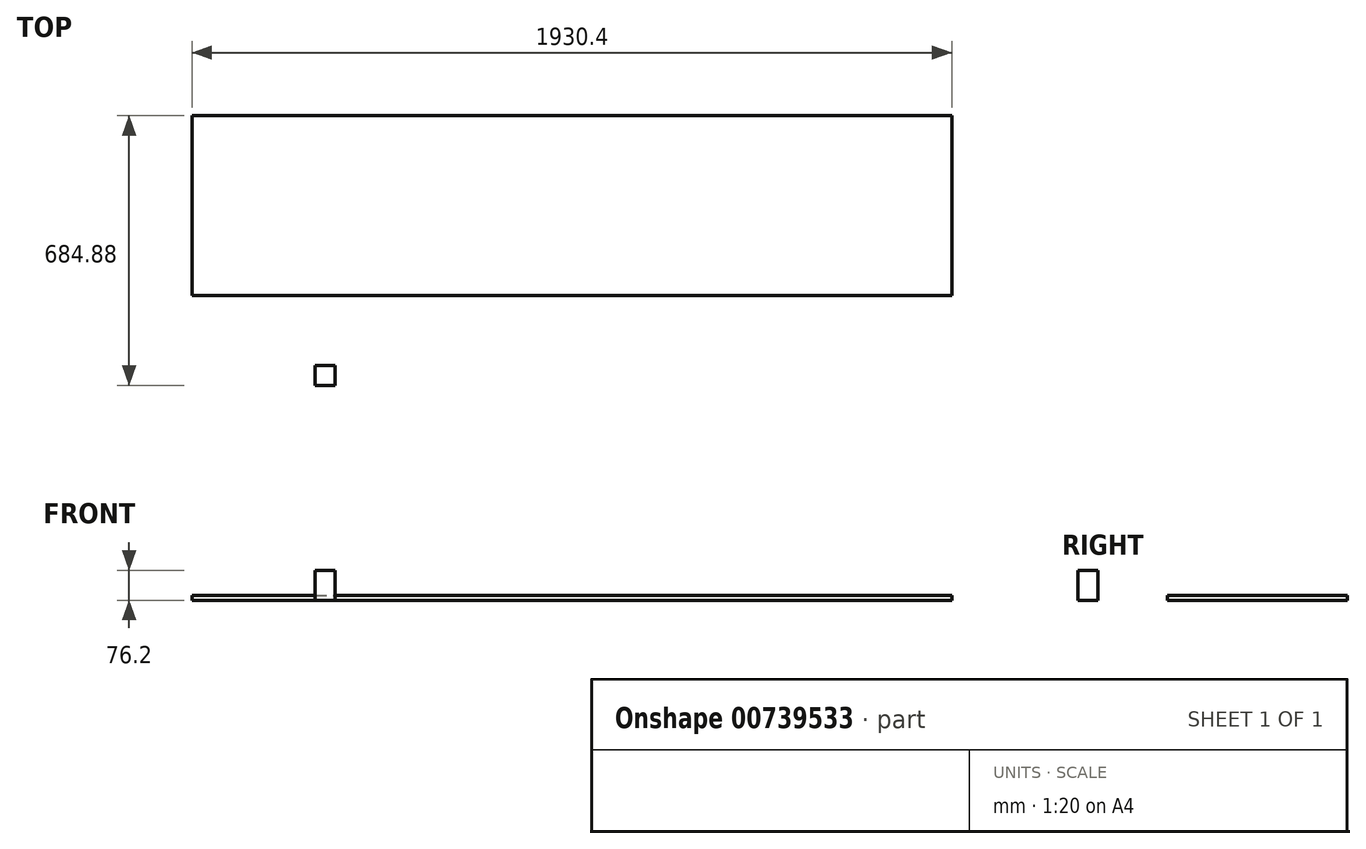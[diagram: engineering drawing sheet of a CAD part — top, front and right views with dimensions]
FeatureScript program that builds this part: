
annotation { "Feature Type Name" : "Feature", "Feature Type Description" : "" }
export const myFeature = defineFeature(function(context is Context, id is Id, definition is map)
    precondition{}
    {
        {
            var Q0;
            Q0=qCreatedBy(makeId("Top.planeOp"),FACE);
            var sketch = newSketch(context, id + "F0", { "sketchPlane" : qUnion([Q0])});
            skLineSegment(sketch, "E0.bottom", {"start": v(-965.2, 228.6) * mm, "end": v(965.2, 228.6) * mm});
            skLineSegment(sketch, "E0.top", {"start": v(-965.2, -228.6) * mm, "end": v(965.2, -228.6) * mm});
            skLineSegment(sketch, "E0.left", {"start": v(-965.2, 228.6) * mm, "end": v(-965.2, -228.6) * mm});
            skLineSegment(sketch, "E0.right", {"start": v(965.2, 228.6) * mm, "end": v(965.2, -228.6) * mm});
            skPoint(sketch, "E0.middle", {"position": v(0, 0) * mm});
            skSolve(sketch);
        }
        {
            var Q0;
            Q0 = qSketchRegion(id + "F0", true);
            extrude(context, id + "F1", {"entities" : qUnion([Q0]), "depth" : 12.7 * mm, "offsetDistance" : 25.4 * mm});
        }
        {
            var Q0;
            Q0=qCreatedBy(makeId("Top.planeOp"),FACE);
            var sketch = newSketch(context, id + "F2", { "sketchPlane" : qUnion([Q0])});
            skLineSegment(sketch, "E1.bottom", {"start": v(-602.16, -456.28) * mm, "end": v(-652.96, -456.28) * mm});
            skLineSegment(sketch, "E1.top", {"start": v(-602.16, -405.48) * mm, "end": v(-652.96, -405.48) * mm});
            skLineSegment(sketch, "E1.left", {"start": v(-602.16, -456.28) * mm, "end": v(-602.16, -405.48) * mm});
            skLineSegment(sketch, "E1.right", {"start": v(-652.96, -456.28) * mm, "end": v(-652.96, -405.48) * mm});
            skPoint(sketch, "E1.middle", {"position": v(-627.56, -430.88) * mm});
            skSolve(sketch);
        }
        {
            var Q0;
            Q0=makeQuery(id+"F2.imprint","IMPRINT",FACE,{"disambiguationData":[TD([[makeQuery(id+"F2.imprint","IMPRINT",EDGE,{"derivedFrom":sQuery(id+"F2.wireOp",EDGE,"E1.bottom")}),-1.0]])]});
            extrude(context, id + "F3", {"entities" : qUnion([Q0]), "depth" : 76.2 * mm, "offsetDistance" : 25.4 * mm});
        }
    });
